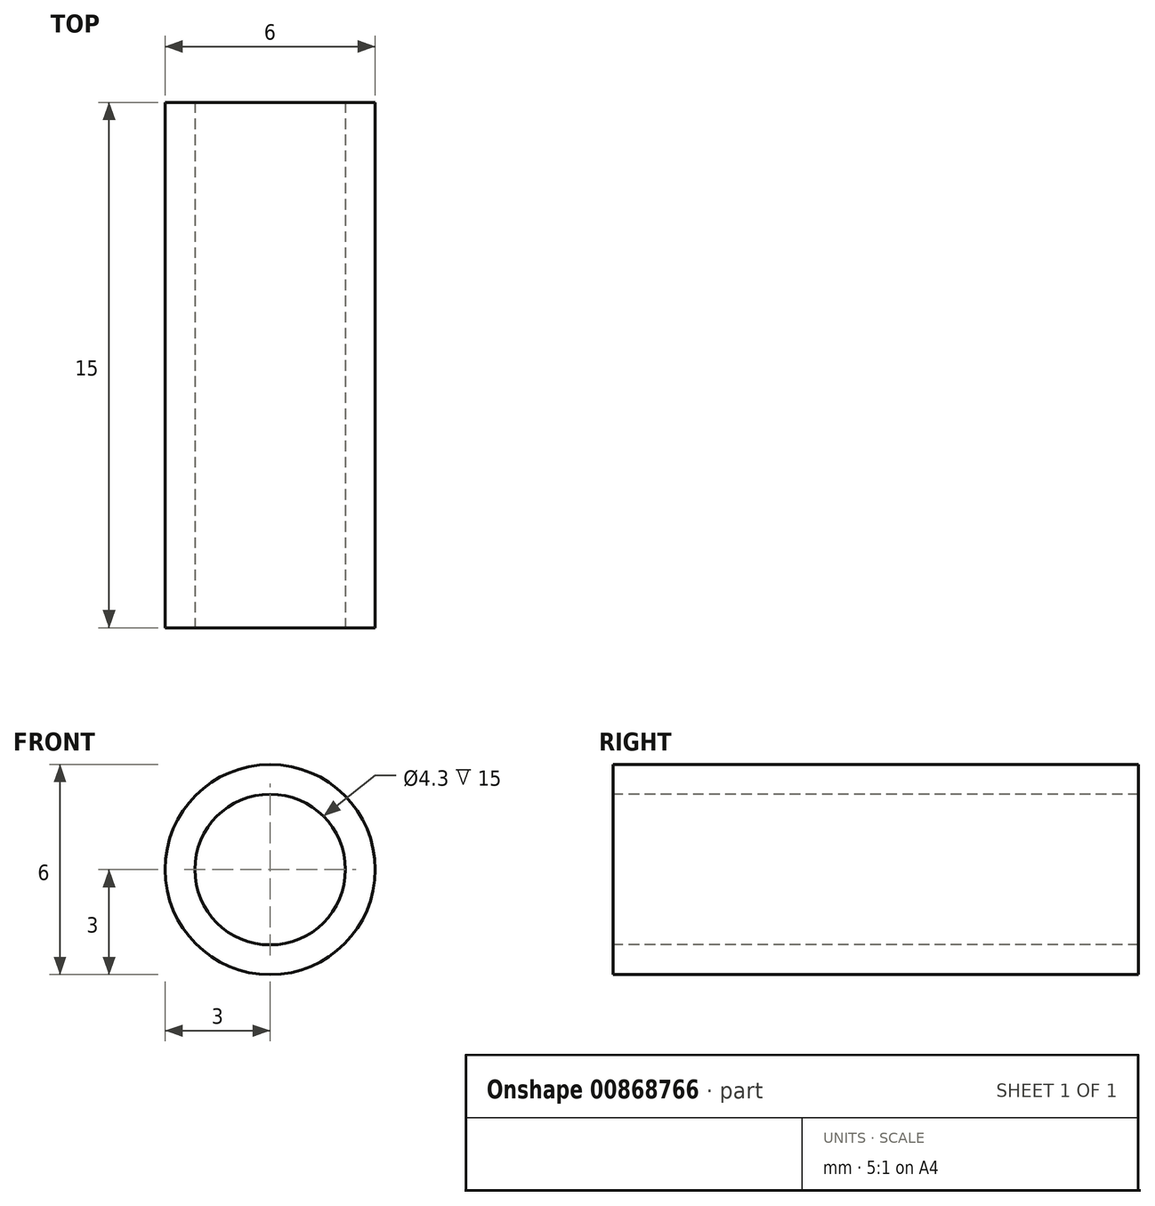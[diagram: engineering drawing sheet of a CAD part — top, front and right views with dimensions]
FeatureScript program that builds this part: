
annotation { "Feature Type Name" : "Feature", "Feature Type Description" : "" }
export const myFeature = defineFeature(function(context is Context, id is Id, definition is map)
    precondition{}
    {
        {
            var Q0;
            Q0=qCreatedBy(makeId("Front.planeOp"),FACE);
            var sketch = newSketch(context, id + "F0", { "sketchPlane" : qUnion([Q0])});
            skCircle(sketch, "E0", {"center": v(0, 0) * mm, "radius": 3 * mm});
            skCircle(sketch, "E1", {"center": v(0, 0) * mm, "radius": 2.15 * mm});
            skSolve(sketch);
        }
        {
            var Q0;
            Q0=makeQuery(id+"F0.imprint","IMPRINT",FACE,{"disambiguationData":[TD([[makeQuery(id+"F0.imprint","IMPRINT",EDGE,{"derivedFrom":sQuery(id+"F0.wireOp",EDGE,"E0")}),1.0]])]});
            extrude(context, id + "F1", {"entities" : qUnion([Q0]), "oppositeDirection" : true, "depth" : 15 * mm, "offsetDistance" : 25 * mm});
        }
    });
